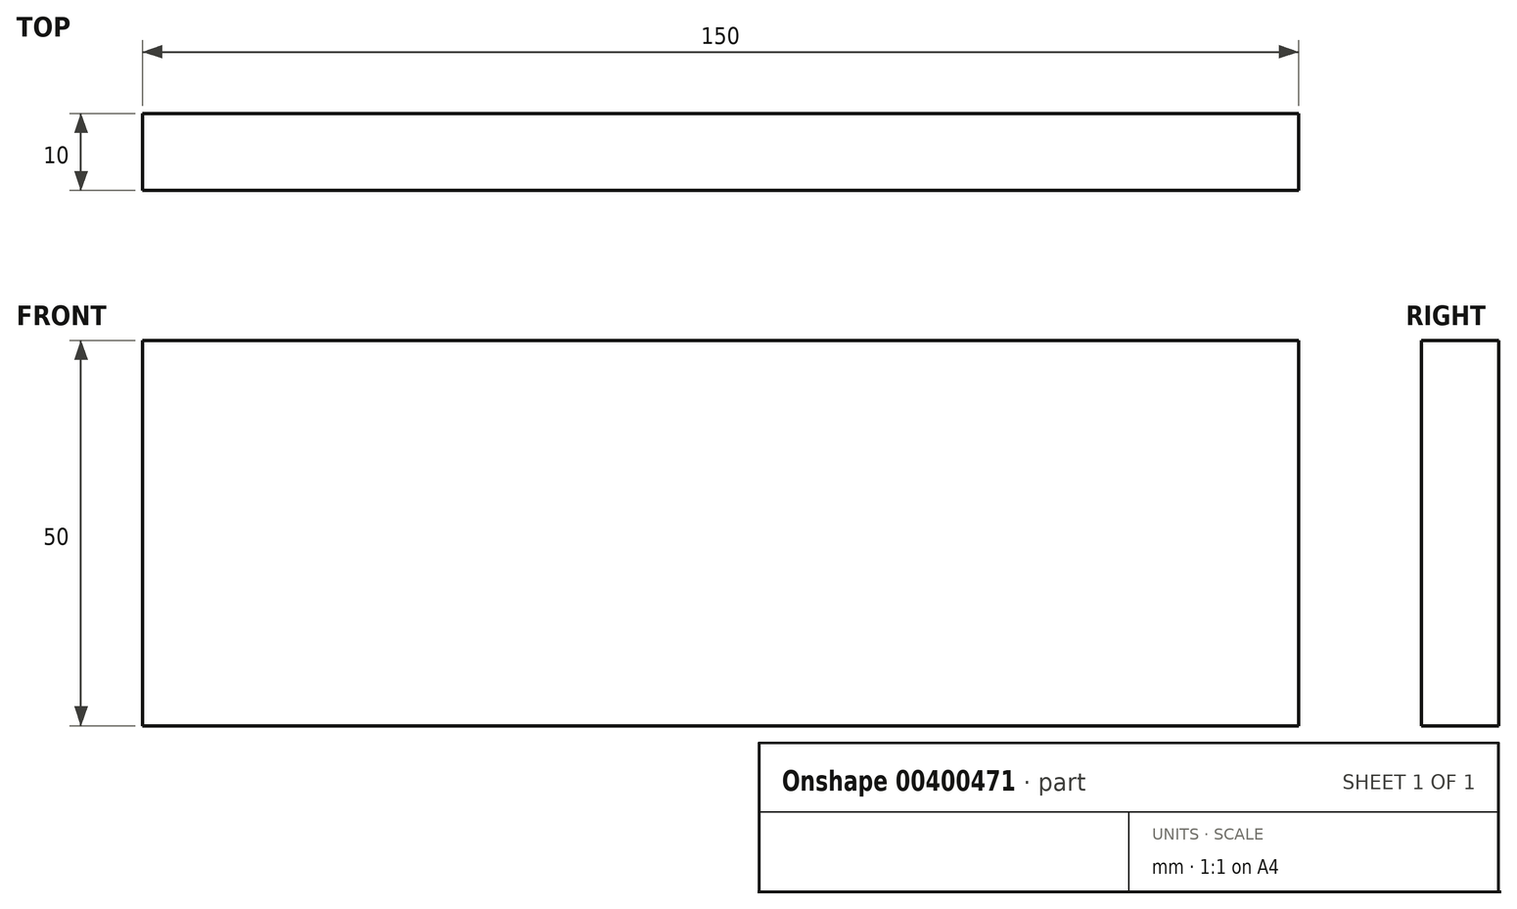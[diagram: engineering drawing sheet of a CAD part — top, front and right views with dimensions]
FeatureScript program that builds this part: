
annotation { "Feature Type Name" : "Feature", "Feature Type Description" : "" }
export const myFeature = defineFeature(function(context is Context, id is Id, definition is map)
    precondition{}
    {
        {
            var Q0;
            Q0=qCreatedBy(makeId("Front.planeOp"),FACE);
            var sketch = newSketch(context, id + "F0", { "sketchPlane" : qUnion([Q0])});
            skLineSegment(sketch, "E0.bottom", {"start": v(0, 0) * mm, "end": v(150, 0) * mm});
            skLineSegment(sketch, "E0.top", {"start": v(0, 50) * mm, "end": v(150, 50) * mm});
            skLineSegment(sketch, "E0.left", {"start": v(0, 0) * mm, "end": v(0, 50) * mm});
            skLineSegment(sketch, "E0.right", {"start": v(150, 0) * mm, "end": v(150, 50) * mm});
            skSolve(sketch);
        }
        {
            var Q0;
            Q0 = qSketchRegion(id + "F0", true);
            extrude(context, id + "F1", {"entities" : qUnion([Q0]), "depth" : 10 * mm});
        }
    });
